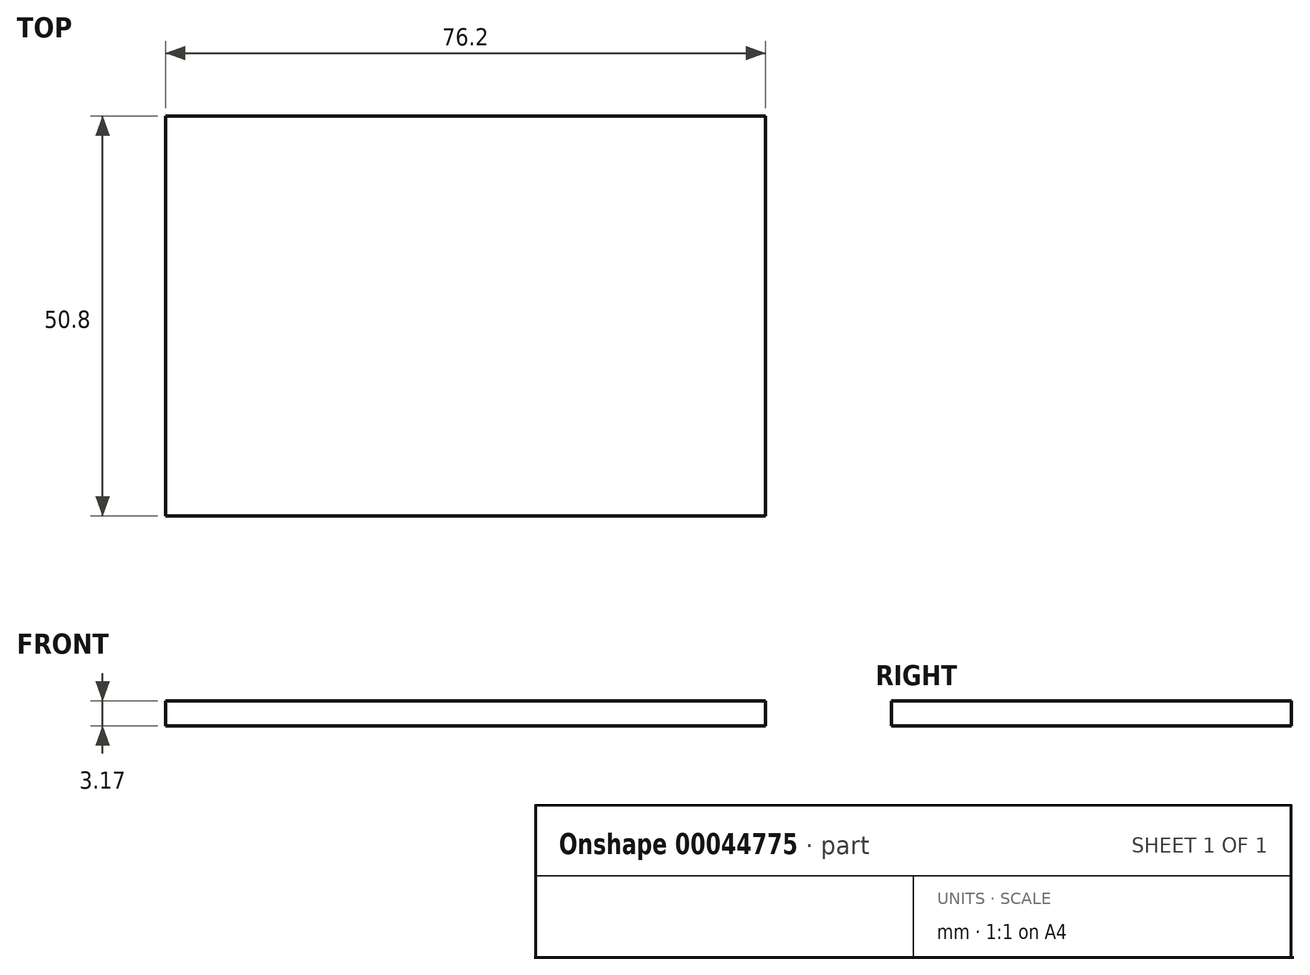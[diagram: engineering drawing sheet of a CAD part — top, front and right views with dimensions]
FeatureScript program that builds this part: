
annotation { "Feature Type Name" : "Feature", "Feature Type Description" : "" }
export const myFeature = defineFeature(function(context is Context, id is Id, definition is map)
    precondition{}
    {
        {
            var Q0;
            Q0=qCreatedBy(makeId("Top.planeOp"),FACE);
            var sketch = newSketch(context, id + "F0", { "sketchPlane" : qUnion([Q0])});
            skLineSegment(sketch, "E0.rect.bottom", {"start": v(38.1, 25.4) * mm, "end": v(-38.1, 25.4) * mm});
            skLineSegment(sketch, "E0.rect.top", {"start": v(38.1, -25.4) * mm, "end": v(-38.1, -25.4) * mm});
            skLineSegment(sketch, "E0.rect.left", {"start": v(38.1, 25.4) * mm, "end": v(38.1, -25.4) * mm});
            skLineSegment(sketch, "E0.rect.right", {"start": v(-38.1, 25.4) * mm, "end": v(-38.1, -25.4) * mm});
            skPoint(sketch, "E0.rect.middle", {"position": v(0, 0) * mm});
            skPoint(sketch, "E1.centerSnap0", {"position": v(-38.1, 0) * mm});
            skSolve(sketch);
        }
        {
            var Q0;
            Q0=makeQuery(id+"F0.imprint","IMPRINT",FACE,{"disambiguationData":[TD([[makeQuery(id+"F0.imprint","IMPRINT",EDGE,{"derivedFrom":sQuery(id+"F0.wireOp",EDGE,"E0.rect.bottom")}),1.0]])]});
            extrude(context, id + "F1", {"entities" : qUnion([Q0]), "depth" : 3.17 * mm});
        }
    });
